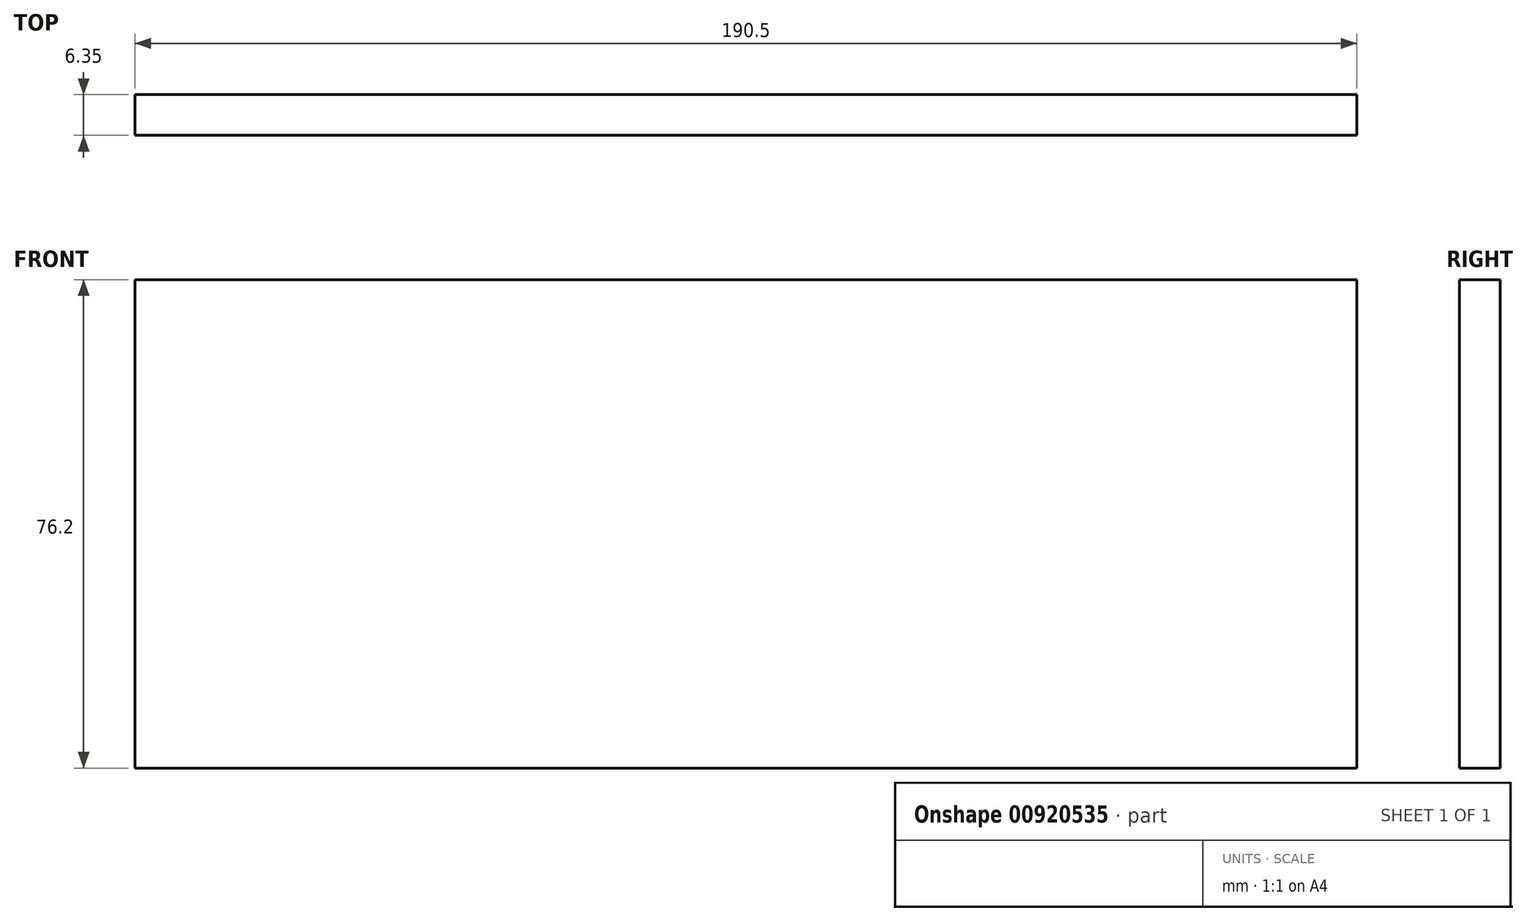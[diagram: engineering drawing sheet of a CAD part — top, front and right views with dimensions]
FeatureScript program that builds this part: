
annotation { "Feature Type Name" : "Feature", "Feature Type Description" : "" }
export const myFeature = defineFeature(function(context is Context, id is Id, definition is map)
    precondition{}
    {
        {
            var Q0;
            Q0=qCreatedBy(makeId("Front.planeOp"),FACE);
            var sketch = newSketch(context, id + "F0", { "sketchPlane" : qUnion([Q0])});
            skLineSegment(sketch, "E0.bottom", {"start": v(0, 38.1) * mm, "end": v(190.5, 38.1) * mm});
            skLineSegment(sketch, "E0.top", {"start": v(0, -38.1) * mm, "end": v(190.5, -38.1) * mm});
            skLineSegment(sketch, "E0.left", {"start": v(0, 38.1) * mm, "end": v(0, -38.1) * mm});
            skLineSegment(sketch, "E0.right", {"start": v(190.5, 38.1) * mm, "end": v(190.5, -38.1) * mm});
            skSolve(sketch);
        }
        {
            var Q0;
            Q0=makeQuery(id+"F0.imprint","IMPRINT",FACE,{"disambiguationData":[TD([[makeQuery(id+"F0.imprint","IMPRINT",EDGE,{"derivedFrom":sQuery(id+"F0.wireOp",EDGE,"E0.bottom")}),-1.0]])]});
            extrude(context, id + "F1", {"entities" : qUnion([Q0]), "oppositeDirection" : true, "depth" : 6.35 * mm, "offsetDistance" : 25.4 * mm});
        }
    });
